# Revit family: GALAD Купер LED
name_source: partatom
category: Осветительные приборы
revit_build: Autodesk Revit 2018 (Build: 20180423_1000(x64)
units: mm (PartAtom-declared; Revit-internal decimal feet)

## family parameters
Источник света = Да
Общий = Нет
Основа = Грань
При загрузке вырезать с полостями = Нет
Размер круглого соединителя = Использовать диаметр
Тип детали = Нормальный
Точка расчета площади = Нет

## types (2) — shared parameters
ADSK_Версия Revit = 2018
ADSK_Версия семейства = 1.01
ADSK_Единица измерения = шт.
ADSK_Завод-изготовитель = АО «КАДОШКИНСКИЙ ЭЛЕКТРОТЕХНИЧЕСКИЙ ЗАВОД»
ADSK_Классификация нагрузок = Освещение
ADSK_Количество = 1
ADSK_Количество фаз = 1
ADSK_Коэффициент мощности = 1
ADSK_Масса = 0.95
ADSK_Масса_Текст = 0.95
ADSK_Напряжение = 230 В
ADSK_Номинальная мощность = 40 В·А
ADSK_Обозначение = ГОСТ 15150-69
ADSK_Полная мощность = 40 В·А
ADSK_Размер_Высота = 66 мм
ADSK_Размер_Длина = 386 мм
ADSK_Размер_Ширина = 156 мм
ADSK_Ток = 0 А
ADSK_Энергоэффективность = 95 лм/Вт
IP = 40
URL = https://galad.ru
Блок аварийного питания = Нет
Видимая форма излучения при визуализации = Нет
Возможный угол наклона = 0
Группа модели = Светильники
Диапазон цветовой температуры = 5028±283
Изготовитель = АО «КАДОШКИНСКИЙ ЭЛЕКТРОТЕХНИЧЕСКИЙ ЗАВОД»
Излучение по длине прямоугольника = 1219 мм
Излучение по ширине прямоугольника = 610 мм
Класс Защиты = 1
Класс защиты от поражения электрическим током = 1
Класс светораспределения = П
Климатическое исполнение = 1…35 °С
Коэффициент пульсации = менее 5%
Материал корпуса = Сталь
Материал рассеивателя = ПММА
Область использования = ЖКХ
Описание = Светодиодный светильник GALAD Купер LED укомплектован датчиком свет+звук, когда освещенности в помещении недостаточно, датчик регистрирует звуки и, при наличии уровня шума выше порогового, включает светильник на 100% мощности, если освещенности в помещении достаточно, светильник не реагирует на звук и остается выключенным.
Отметка по умолчанию = 1219 мм
Полная установленная мощность = 40 В·А
Световая отдача = 95
Светофильтр = 16777215
Смещение цветовой температуры при затухании лампы = <Нет>
Снижение светового потока во время разгорания = не более 6%
Срок службы = 12 лет
Тип КСС = Косинусная
Тип ПРА = ЭПРА
Тип источника света = LED
Тип монтажной поверхности = настенный
Тип продукции = Светильник
Тип устройства управления светодиодами = без управления
Угол наклона = 90.00°
Цветопередача = 80
Частота = 50
zero-valued in all types: Неравномерность яркости

## per-type parameters (varying)
| type | ADSK_Код изделия | Климатическая зона | Файл фотометрической сетки |
| ДБО64-6х2-004 УХЛ4 (220В с датчиком.) | 2654 | УХЛ5 | GALAD kuper dbo64-6X2-004.IES |
| ДБО64-6х2-002 УХЛ4 (220В) | 2641 | УХЛ4 | GALAD kuper dbo64-6X2-002.IES |

note: column(s) folded — value = type name in every type: ADSK_Марка, ADSK_Наименование, ADSK_Наименование краткое
